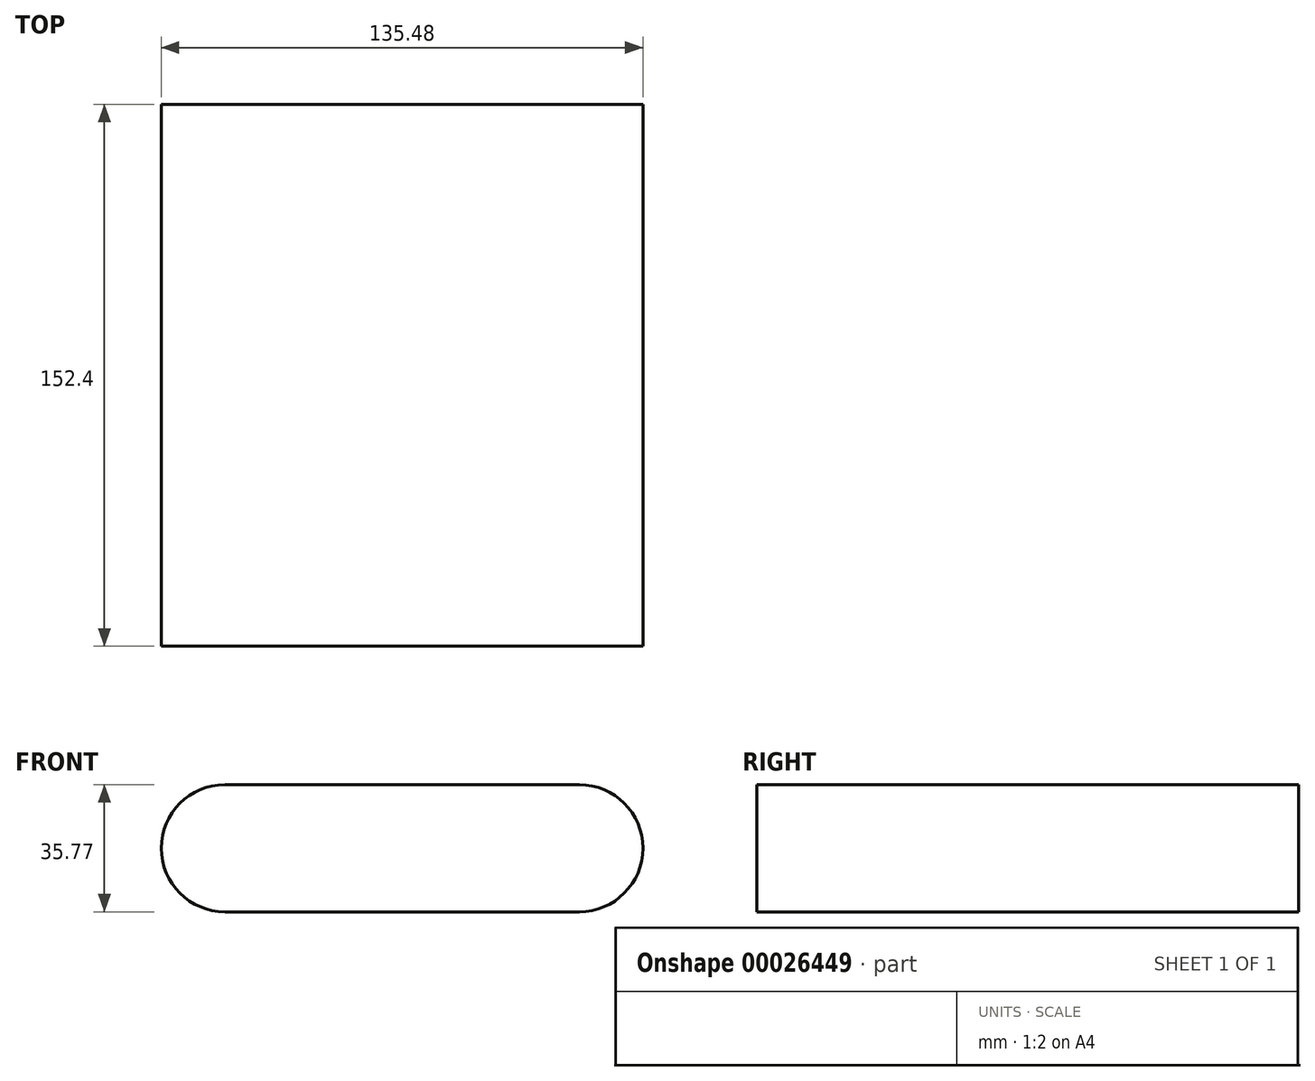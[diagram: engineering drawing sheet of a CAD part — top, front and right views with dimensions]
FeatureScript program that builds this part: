
annotation { "Feature Type Name" : "Feature", "Feature Type Description" : "" }
export const myFeature = defineFeature(function(context is Context, id is Id, definition is map)
    precondition{}
    {
        {
            var Q0;
            Q0=qCreatedBy(makeId("Front.planeOp"),FACE);
            var sketch = newSketch(context, id + "F0", { "sketchPlane" : qUnion([Q0])});
            skLineSegment(sketch, "E0.rect.bottom", {"start": v(16.28, -8.47) * mm, "end": v(-83.42, -8.47) * mm});
            skLineSegment(sketch, "E0.rect.top", {"start": v(16.28, 27.3) * mm, "end": v(-83.42, 27.3) * mm});
            skLineSegment(sketch, "E0.rect.left", {"start": v(16.28, -8.47) * mm, "end": v(16.28, 27.3) * mm});
            skLineSegment(sketch, "E0.rect.right", {"start": v(-83.42, -8.47) * mm, "end": v(-83.42, 27.3) * mm});
            skPoint(sketch, "E0.rect.middle", {"position": v(-33.57, 9.42) * mm});
            skArc(sketch, "E1", {"start": v(16.28, -8.47) * mm, "mid": v(34.17, 9.42) * mm, "end": v(16.28, 27.3) * mm});
            skArc(sketch, "E2", {"start": v(-83.42, 27.3) * mm, "mid": v(-101.3, 9.42) * mm, "end": v(-83.42, -8.47) * mm});
            skSolve(sketch);
        }
        {
            var Q0;
            Q0 = qSketchRegion(id + "F0", true);
            extrude(context, id + "F1", {"entities" : qUnion([Q0]), "endBound" : BoundingType.SYMMETRIC, "depth" : 152.4 * mm});
        }
    });
